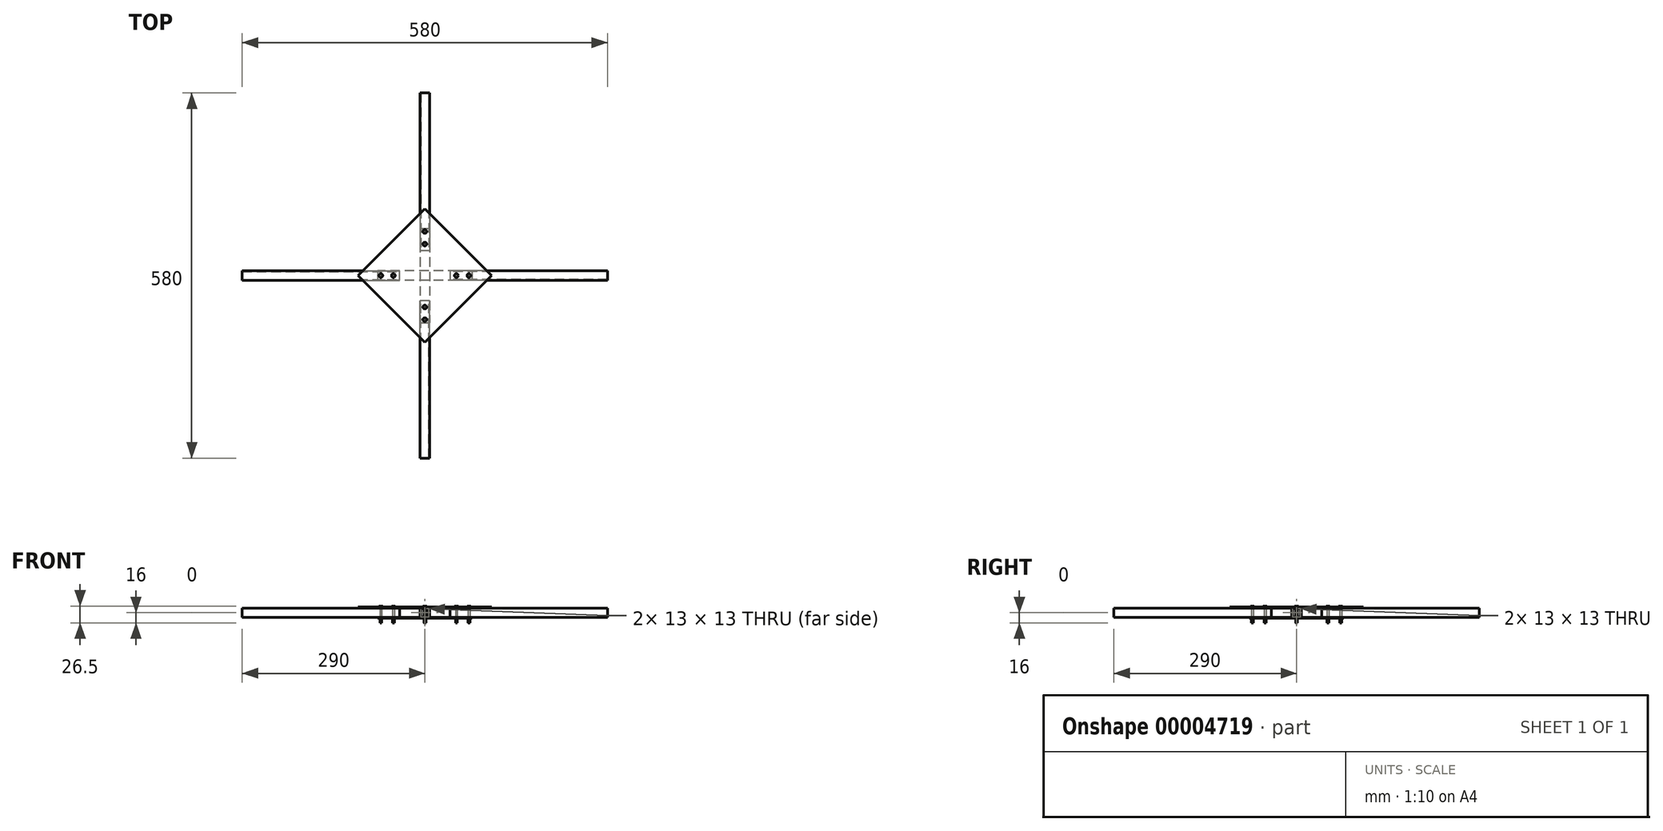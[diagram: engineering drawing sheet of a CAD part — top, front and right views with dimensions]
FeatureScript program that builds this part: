
annotation { "Feature Type Name" : "Feature", "Feature Type Description" : "" }
export const myFeature = defineFeature(function(context is Context, id is Id, definition is map)
    precondition{}
    {
        {
            var Q0;
            Q0=qCreatedBy(makeId("Right.planeOp"),FACE);
            var sketch = newSketch(context, id + "F0", { "sketchPlane" : qUnion([Q0])});
            skLineSegment(sketch, "E0.rect.bottom", {"start": v(6.5, -6.5) * mm, "end": v(-6.5, -6.5) * mm});
            skLineSegment(sketch, "E0.rect.top", {"start": v(6.5, 6.5) * mm, "end": v(-6.5, 6.5) * mm});
            skLineSegment(sketch, "E0.rect.left", {"start": v(6.5, -6.5) * mm, "end": v(6.5, 6.5) * mm});
            skLineSegment(sketch, "E0.rect.right", {"start": v(-6.5, -6.5) * mm, "end": v(-6.5, 6.5) * mm});
            skPoint(sketch, "E0.rect.middle", {"position": v(0, 0) * mm});
            skLineSegment(sketch, "E1.rect.bottom", {"start": v(7.5, 7.5) * mm, "end": v(-7.5, 7.5) * mm});
            skLineSegment(sketch, "E1.rect.top", {"start": v(7.5, -7.5) * mm, "end": v(-7.5, -7.5) * mm});
            skLineSegment(sketch, "E1.rect.left", {"start": v(7.5, 7.5) * mm, "end": v(7.5, -7.5) * mm});
            skLineSegment(sketch, "E1.rect.right", {"start": v(-7.5, 7.5) * mm, "end": v(-7.5, -7.5) * mm});
            skLineSegment(sketch, "E2", {"start": v(0, 0) * mm, "end": v(-51.77, 0) * mm, "construction": true});
            skLineSegment(sketch, "E3", {"start": v(0, 0) * mm, "end": v(0, 56.47) * mm, "construction": true});
            skSolve(sketch);
        }
        {
            var Q0;
            Q0 = qSketchRegion(id + "F0", true);
            extrude(context, id + "F1", {"entities" : qUnion([Q0]), "depth" : 250 * mm});
        }
        {
            var Q0;
            Q0=makeQuery(id+"F1.opExtrude","SWEPT_BODY",BODY,{"disambiguationData":[OSD([sQuery(id+"F0.wireOp",EDGE,"E0.rect.bottom"),sQuery(id+"F0.wireOp",EDGE,"E0.rect.top"),sQuery(id+"F0.wireOp",EDGE,"E0.rect.left"),sQuery(id+"F0.wireOp",EDGE,"E0.rect.right"),sQuery(id+"F0.wireOp",EDGE,"E1.rect.bottom"),sQuery(id+"F0.wireOp",EDGE,"E1.rect.top"),sQuery(id+"F0.wireOp",EDGE,"E1.rect.left"),sQuery(id+"F0.wireOp",EDGE,"E1.rect.right")])]});
            transform(context, id + "F2", {"entities" : qUnion([Q0]), "transformType" : TransformType.TRANSLATION_3D, "dx" : 40 * mm, "dy" : 0 * mm, "dz" : 0 * mm, "makeCopy" : false});
        }
        {
            var Q0;
            Q0=makeQuery(id+"F1.opExtrude","SWEPT_BODY",BODY,{"disambiguationData":[OSD([sQuery(id+"F0.wireOp",EDGE,"E0.rect.bottom"),sQuery(id+"F0.wireOp",EDGE,"E0.rect.top"),sQuery(id+"F0.wireOp",EDGE,"E0.rect.left"),sQuery(id+"F0.wireOp",EDGE,"E0.rect.right"),sQuery(id+"F0.wireOp",EDGE,"E1.rect.bottom"),sQuery(id+"F0.wireOp",EDGE,"E1.rect.top"),sQuery(id+"F0.wireOp",EDGE,"E1.rect.left"),sQuery(id+"F0.wireOp",EDGE,"E1.rect.right")])]});
            var Q1;
            Q1=sQuery(id+"F0.wireOp",EDGE,"E3");
            circularPattern(context, id + "F3", {"entities" : qUnion([Q0]), "axis" : qUnion([Q1]), "angle" : 90 * degree, "instanceCount" : 4});
        }
        {
            var Q0;
            Q0=makeQuery(id+"F3.opPattern","COPY",FACE,{"derivedFrom":makeQuery(id+"F1.opExtrude","SWEPT_FACE",FACE,{"disambiguationData":[OSD([sQuery(id+"F0.wireOp",EDGE,"E1.rect.bottom")])]}),"instanceName":"2"});
            var sketch = newSketch(context, id + "F4", { "sketchPlane" : qUnion([Q0])});
            skLineSegment(sketch, "E4.rect.bottom", {"start": v(75, -75) * mm, "end": v(-75, -75) * mm});
            skLineSegment(sketch, "E4.rect.top", {"start": v(75, 75) * mm, "end": v(-75, 75) * mm});
            skLineSegment(sketch, "E4.rect.left", {"start": v(75, -75) * mm, "end": v(75, 75) * mm});
            skLineSegment(sketch, "E4.rect.right", {"start": v(-75, -75) * mm, "end": v(-75, 75) * mm});
            skPoint(sketch, "E4.rect.middle", {"position": v(0, 0) * mm});
            skSolve(sketch);
        }
        {
            var Q0;
            Q0 = qSketchRegion(id + "F4", true);
            extrude(context, id + "F5", {"entities" : qUnion([Q0]), "depth" : 1.5 * mm});
        }
        {
            var Q0;
            Q0=makeQuery(id+"F3.opPattern","COPY",FACE,{"derivedFrom":makeQuery(id+"F1.opExtrude","SWEPT_FACE",FACE,{"disambiguationData":[OSD([sQuery(id+"F0.wireOp",EDGE,"E1.rect.top")])]}),"instanceName":"1"});
            var sketch = newSketch(context, id + "F6", { "sketchPlane" : qUnion([Q0])});
            skLineSegment(sketch, "E5.rect.bottom", {"start": v(75, -7.5) * mm, "end": v(-75, -7.5) * mm});
            skLineSegment(sketch, "E5.rect.top", {"start": v(75, 7.5) * mm, "end": v(-75, 7.5) * mm});
            skLineSegment(sketch, "E5.rect.left", {"start": v(75, -7.5) * mm, "end": v(75, 7.5) * mm});
            skLineSegment(sketch, "E5.rect.right", {"start": v(-75, -7.5) * mm, "end": v(-75, 7.5) * mm});
            skPoint(sketch, "E5.rect.middle", {"position": v(0, 0) * mm});
            skSolve(sketch);
        }
        {
            var Q0;
            Q0 = qSketchRegion(id + "F6", true);
            extrude(context, id + "F7", {"entities" : qUnion([Q0]), "depth" : 1.5 * mm});
        }
        {
            var Q0;
            Q0=makeQuery(id+"F5.opExtrude","SWEPT_BODY",BODY,{"disambiguationData":[OSD([sQuery(id+"F4.wireOp",EDGE,"E4.rect.bottom"),sQuery(id+"F4.wireOp",EDGE,"E4.rect.top"),sQuery(id+"F4.wireOp",EDGE,"E4.rect.left"),sQuery(id+"F4.wireOp",EDGE,"E4.rect.right")])]});
            var Q1;
            Q1=sQuery(id+"F0.wireOp",EDGE,"E3");
            transform(context, id + "F8", {"entities" : qUnion([Q0]), "transformType" : TransformType.ROTATION, "transformAxis" : qUnion([Q1]), "angle" : 45 * degree, "makeCopy" : false});
        }
        {
            var Q0;
            Q0=makeQuery(id+"F7.opExtrude","SWEPT_BODY",BODY,{"disambiguationData":[OSD([sQuery(id+"F6.wireOp",EDGE,"E5.rect.bottom"),sQuery(id+"F6.wireOp",EDGE,"E5.rect.top"),sQuery(id+"F6.wireOp",EDGE,"E5.rect.left"),sQuery(id+"F6.wireOp",EDGE,"E5.rect.right")])]});
            var Q1;
            Q1=sQuery(id+"F0.wireOp",EDGE,"E3");
            circularPattern(context, id + "F9", {"entities" : qUnion([Q0]), "axis" : qUnion([Q1]), "angle" : 90 * degree, "instanceCount" : 2});
        }
        {
            var Q0;
            Q0=qCreatedBy(makeId("Front.planeOp"),FACE);
            var sketch = newSketch(context, id + "F10", { "sketchPlane" : qUnion([Q0])});
            skLineSegment(sketch, "E6", {"start": v(0, 10.5) * mm, "end": v(3, 10.5) * mm});
            skLineSegment(sketch, "E7", {"start": v(3, 10.5) * mm, "end": v(3, 9) * mm});
            skLineSegment(sketch, "E8", {"start": v(3, 9) * mm, "end": v(1.5, 9) * mm});
            skLineSegment(sketch, "E9", {"start": v(1.5, 9) * mm, "end": v(1.5, -16) * mm});
            skLineSegment(sketch, "E10", {"start": v(1.5, -16) * mm, "end": v(0, -16) * mm});
            skLineSegment(sketch, "E11", {"start": v(0, 10.5) * mm, "end": v(0, -16) * mm});
            skSolve(sketch);
        }
        {
            var Q0;
            Q0 = qSketchRegion(id + "F10", true);
            var Q1;
            Q1=sQuery(id+"F0.wireOp",EDGE,"E3");
            revolve(context, id + "F11", {"entities" : qUnion([Q0]), "axis" : qUnion([Q1]), "revolveType" : RevolveType.FULL});
        }
        {
            var Q0;
            Q0=makeQuery(id+"F11.opRevolve","SWEPT_BODY",BODY,{"disambiguationData":[OSD([sQuery(id+"F10.wireOp",EDGE,"E6"),sQuery(id+"F10.wireOp",EDGE,"E7"),sQuery(id+"F10.wireOp",EDGE,"E8"),sQuery(id+"F10.wireOp",EDGE,"E9"),sQuery(id+"F10.wireOp",EDGE,"E10"),sQuery(id+"F10.wireOp",EDGE,"E11")])]});
            transform(context, id + "F12", {"entities" : qUnion([Q0]), "transformType" : TransformType.TRANSLATION_3D, "dx" : 50 * mm, "dy" : 0 * mm, "dz" : 0 * mm, "makeCopy" : false});
        }
        {
            var Q0;
            Q0=makeQuery(id+"F11.opRevolve","SWEPT_BODY",BODY,{"disambiguationData":[OSD([sQuery(id+"F10.wireOp",EDGE,"E6"),sQuery(id+"F10.wireOp",EDGE,"E7"),sQuery(id+"F10.wireOp",EDGE,"E8"),sQuery(id+"F10.wireOp",EDGE,"E9"),sQuery(id+"F10.wireOp",EDGE,"E10"),sQuery(id+"F10.wireOp",EDGE,"E11")])]});
            transform(context, id + "F13", {"entities" : qUnion([Q0]), "transformType" : TransformType.TRANSLATION_3D, "dx" : 20 * mm, "dy" : 0 * mm, "dz" : 0 * mm, "makeCopy" : true});
        }
        {
            var Q0;
            Q0=makeQuery(id+"F11.opRevolve","SWEPT_BODY",BODY,{"disambiguationData":[OSD([sQuery(id+"F10.wireOp",EDGE,"E6"),sQuery(id+"F10.wireOp",EDGE,"E7"),sQuery(id+"F10.wireOp",EDGE,"E8"),sQuery(id+"F10.wireOp",EDGE,"E9"),sQuery(id+"F10.wireOp",EDGE,"E10"),sQuery(id+"F10.wireOp",EDGE,"E11")])]});
            var Q1;
            Q1=makeQuery(id+"F13.opPattern","COPY",BODY,{"derivedFrom":makeQuery(id+"F11.opRevolve","SWEPT_BODY",BODY,{"disambiguationData":[OSD([sQuery(id+"F10.wireOp",EDGE,"E6"),sQuery(id+"F10.wireOp",EDGE,"E7"),sQuery(id+"F10.wireOp",EDGE,"E8"),sQuery(id+"F10.wireOp",EDGE,"E9"),sQuery(id+"F10.wireOp",EDGE,"E10"),sQuery(id+"F10.wireOp",EDGE,"E11")])]}),"instanceName":"1"});
            var Q2;
            Q2=sQuery(id+"F0.wireOp",EDGE,"E3");
            circularPattern(context, id + "F14", {"entities" : qUnion([Q0, Q1]), "axis" : qUnion([Q2]), "angle" : 90 * degree, "instanceCount" : 4});
        }
    });
